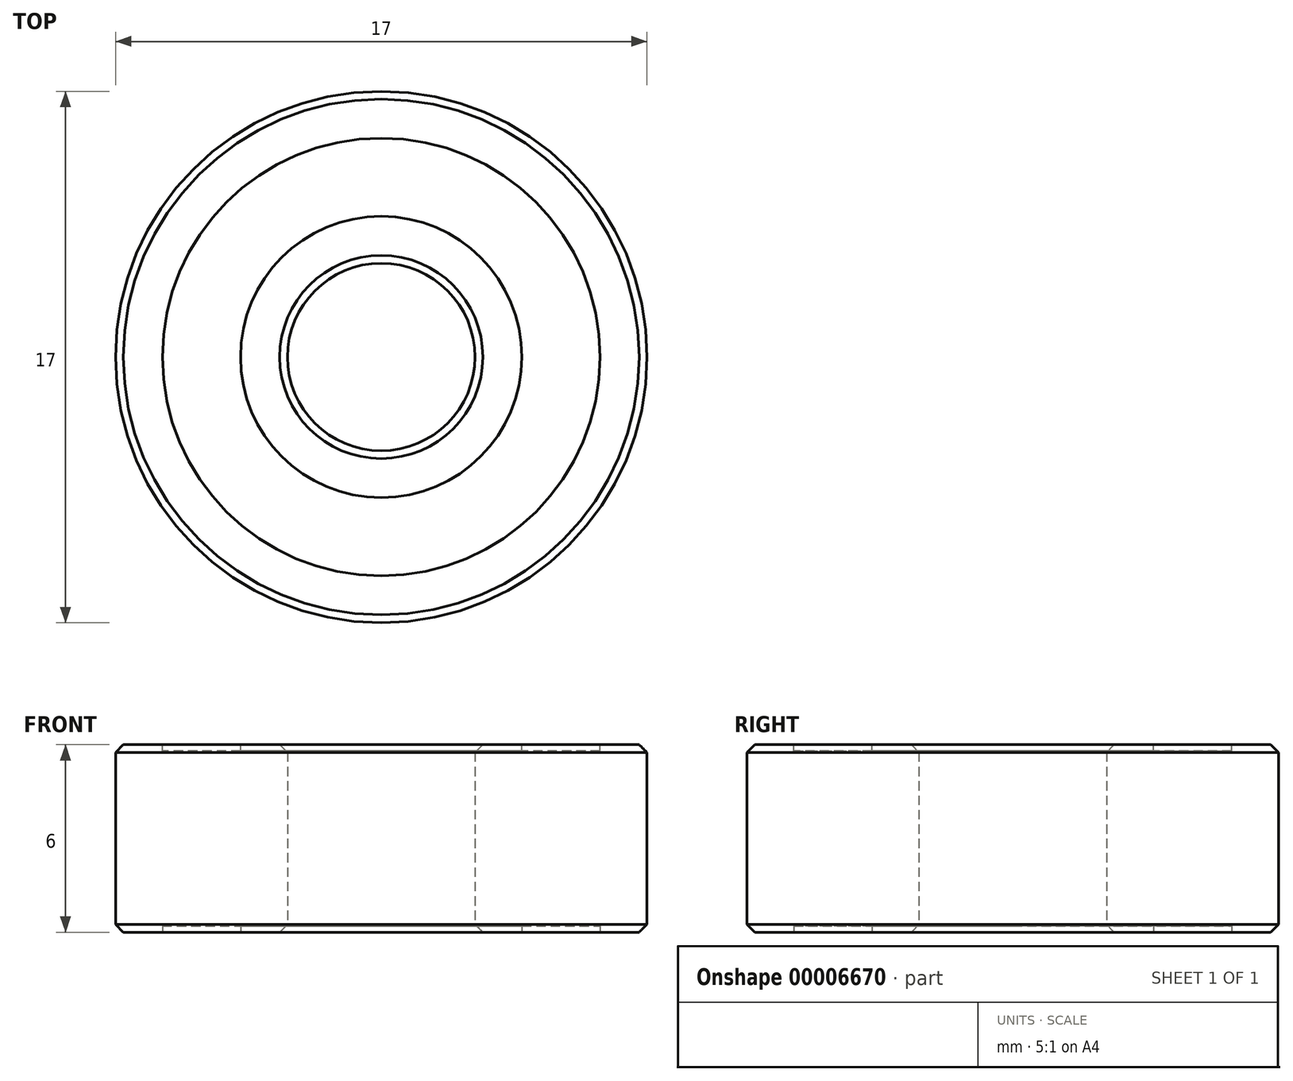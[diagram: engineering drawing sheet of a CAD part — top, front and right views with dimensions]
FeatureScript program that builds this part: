
annotation { "Feature Type Name" : "Feature", "Feature Type Description" : "" }
export const myFeature = defineFeature(function(context is Context, id is Id, definition is map)
    precondition{}
    {
        {
            var Q0;
            Q0=qCreatedBy(makeId("Top.planeOp"),FACE);
            var sketch = newSketch(context, id + "F0", { "sketchPlane" : qUnion([Q0])});
            skCircle(sketch, "E0", {"center": v(0, 0) * mm, "radius": 8.5 * mm});
            skCircle(sketch, "E1", {"center": v(0, 0) * mm, "radius": 3 * mm});
            skSolve(sketch);
        }
        {
            var Q0;
            Q0 = qSketchRegion(id + "F0", true);
            extrude(context, id + "F1", {"entities" : qUnion([Q0]), "depth" : 6 * mm});
        }
        {
            var Q0;
            Q0=makeQuery(id+"F1.opExtrude","CAP_FACE",FACE,{"disambiguationData":[OSD([sQuery(id+"F0.wireOp",EDGE,"E0"),sQuery(id+"F0.wireOp",EDGE,"E1")])],"isStart":false});
            var sketch = newSketch(context, id + "F2", { "sketchPlane" : qUnion([Q0])});
            skCircle(sketch, "E2", {"center": v(0, 0) * mm, "radius": 7 * mm});
            skCircle(sketch, "E3", {"center": v(0, 0) * mm, "radius": 4.5 * mm});
            skSolve(sketch);
        }
        {
            var Q0;
            Q0 = qSketchRegion(id + "F2", true);
            extrude(context, id + "F3", {"entities" : qUnion([Q0]), "operationType" : NewBodyOperationType.REMOVE, "oppositeDirection" : true, "depth" : 0.2 * mm});
        }
        {
            var Q0;
            Q0=makeQuery(id+"F1.opExtrude","CAP_EDGE",EDGE,{"disambiguationData":[OSD([sQuery(id+"F0.wireOp",EDGE,"E0")])],"isStart":false});
            var Q1;
            Q1=makeQuery(id+"F1.opExtrude","CAP_EDGE",EDGE,{"disambiguationData":[OSD([sQuery(id+"F0.wireOp",EDGE,"E1")])],"isStart":false});
            var Q2;
            Q2=makeQuery(id+"F1.opExtrude","CAP_EDGE",EDGE,{"disambiguationData":[OSD([sQuery(id+"F0.wireOp",EDGE,"E0")])],"isStart":true});
            var Q3;
            Q3=makeQuery(id+"F1.opExtrude","CAP_EDGE",EDGE,{"disambiguationData":[OSD([sQuery(id+"F0.wireOp",EDGE,"E1")])],"isStart":true});
            chamfer(context, id + "F4", {"entities" : qUnion([Q0, Q1, Q2, Q3]), "width" : 0.25 * mm, "tangentPropagation" : true});
        }
        {
            var Q0;
            Q0=makeQuery(id+"F1.opExtrude","CAP_FACE",FACE,{"disambiguationData":[OSD([sQuery(id+"F0.wireOp",EDGE,"E0"),sQuery(id+"F0.wireOp",EDGE,"E1")])],"isStart":true});
            var sketch = newSketch(context, id + "F5", { "sketchPlane" : qUnion([Q0])});
            skCircle(sketch, "E4", {"center": v(0, 0) * mm, "radius": 7 * mm});
            skCircle(sketch, "E5", {"center": v(0, 0) * mm, "radius": 4.5 * mm});
            skSolve(sketch);
        }
        {
            var Q0;
            Q0 = qSketchRegion(id + "F5", true);
            extrude(context, id + "F6", {"entities" : qUnion([Q0]), "operationType" : NewBodyOperationType.REMOVE, "oppositeDirection" : true, "depth" : 0.2 * mm});
        }
    });
